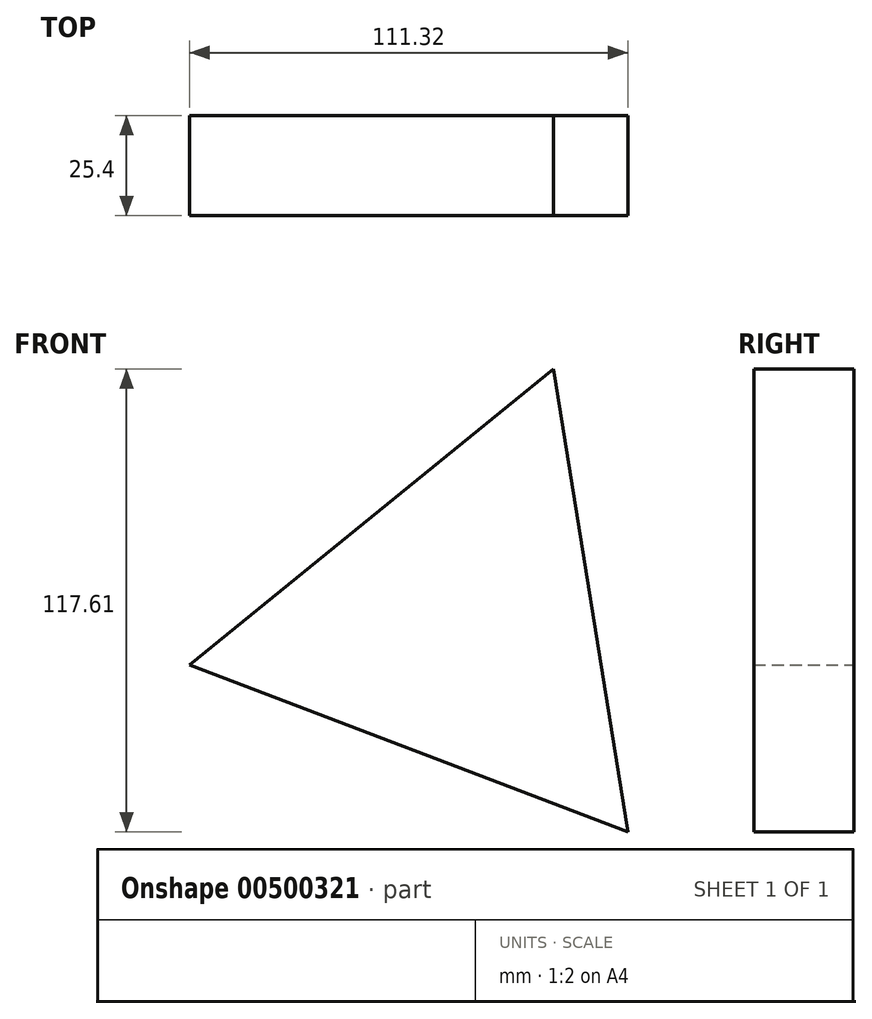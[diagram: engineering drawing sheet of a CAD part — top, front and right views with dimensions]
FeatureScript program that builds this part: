
annotation { "Feature Type Name" : "Feature", "Feature Type Description" : "" }
export const myFeature = defineFeature(function(context is Context, id is Id, definition is map)
    precondition{}
    {
        {
            var Q0;
            Q0=qCreatedBy(makeId("Front.planeOp"),FACE);
            var sketch = newSketch(context, id + "F0", { "sketchPlane" : qUnion([Q0])});
            skCircle(sketch, "E0.cCircle", {"center": v(0, 0) * mm, "radius": 68.78 * mm, "construction": true});
            skLineSegment(sketch, "E0.0", {"start": v(24.48, 64.27) * mm, "end": v(43.42, -53.34) * mm});
            skLineSegment(sketch, "E0.1", {"start": v(43.42, -53.34) * mm, "end": v(-67.9, -10.93) * mm});
            skLineSegment(sketch, "E0.2", {"start": v(-67.9, -10.93) * mm, "end": v(24.48, 64.27) * mm});
            skSolve(sketch);
        }
        {
            var Q0;
            Q0=makeQuery(id+"F0.imprint","IMPRINT",FACE,{"disambiguationData":[TD([[makeQuery(id+"F0.imprint","IMPRINT",EDGE,{"derivedFrom":sQuery(id+"F0.wireOp",EDGE,"E0.0")}),-1.0]])]});
            extrude(context, id + "F1", {"entities" : qUnion([Q0]), "depth" : 25.4 * mm});
        }
    });
